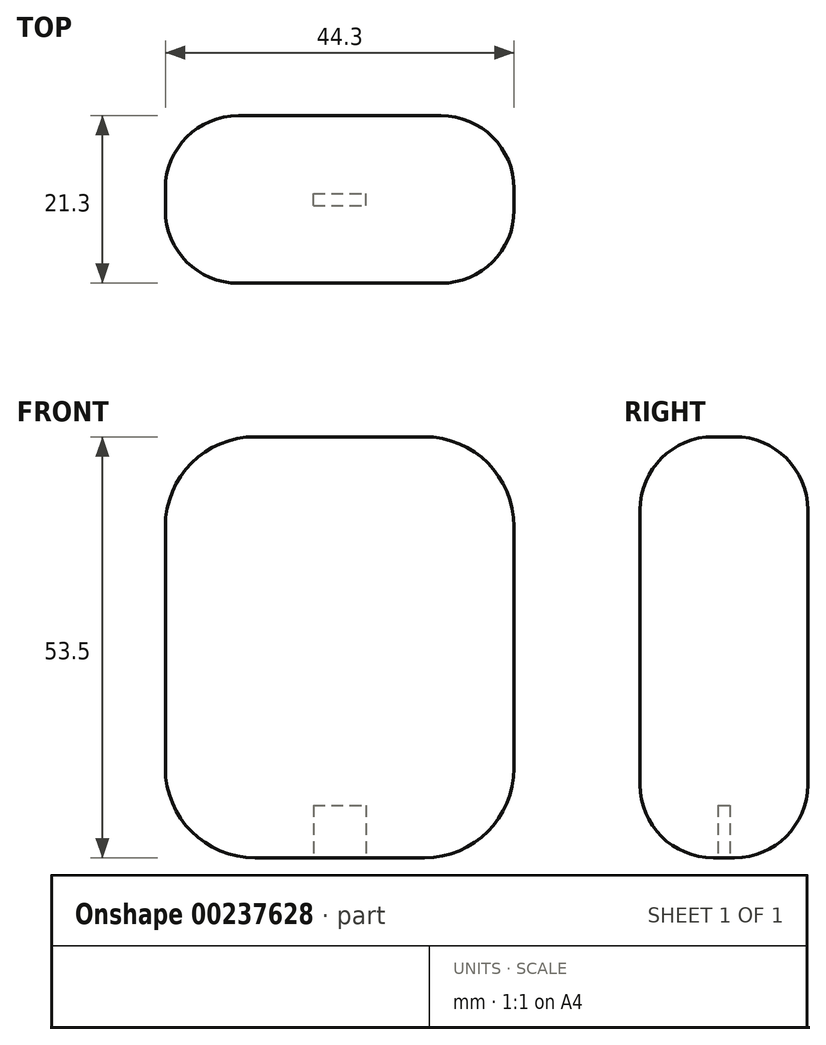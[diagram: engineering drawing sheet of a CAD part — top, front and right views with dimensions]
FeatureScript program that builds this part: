
annotation { "Feature Type Name" : "Feature", "Feature Type Description" : "" }
export const myFeature = defineFeature(function(context is Context, id is Id, definition is map)
    precondition{}
    {
        {
            var Q0;
            Q0=qCreatedBy(makeId("Front.planeOp"),FACE);
            var sketch = newSketch(context, id + "F0", { "sketchPlane" : qUnion([Q0])});
            skLineSegment(sketch, "E0.bottom", {"start": v(0, 0) * mm, "end": v(44.3, 0) * mm});
            skLineSegment(sketch, "E0.top", {"start": v(0, 53.5) * mm, "end": v(44.3, 53.5) * mm});
            skLineSegment(sketch, "E0.left", {"start": v(0, 0) * mm, "end": v(0, 53.5) * mm});
            skLineSegment(sketch, "E0.right", {"start": v(44.3, 0) * mm, "end": v(44.3, 53.5) * mm});
            skSolve(sketch);
        }
        {
            var Q0;
            Q0=makeQuery(id+"F0.imprint","IMPRINT",FACE,{"disambiguationData":[TD([[makeQuery(id+"F0.imprint","IMPRINT",EDGE,{"derivedFrom":sQuery(id+"F0.wireOp",EDGE,"E0.bottom")}),1.0]])]});
            extrude(context, id + "F1", {"entities" : qUnion([Q0]), "depth" : 21.3 * mm});
        }
        {
            var Q0;
            Q0=makeQuery(id+"F1.opExtrude","SWEPT_EDGE",EDGE,{"disambiguationData":[OSD([sQuery(id+"F0.wireOp",EDGE,"E0.bottom"),sQuery(id+"F0.wireOp",EDGE,"E0.right")])]});
            fillet(context, id + "F2", {"entities" : qUnion([Q0]), "radius" : 11.4 * mm, "tangentPropagation" : true, "allowEdgeOverflow" : false});
        }
        {
            var Q0;
            Q0=makeQuery(id+"F1.opExtrude","SWEPT_EDGE",EDGE,{"disambiguationData":[OSD([sQuery(id+"F0.wireOp",EDGE,"E0.bottom"),sQuery(id+"F0.wireOp",EDGE,"E0.left")])]});
            fillet(context, id + "F3", {"entities" : qUnion([Q0]), "radius" : 11.4 * mm, "tangentPropagation" : true, "allowEdgeOverflow" : false});
        }
        {
            var Q0;
            Q0=makeQuery(id+"F1.opExtrude","SWEPT_EDGE",EDGE,{"disambiguationData":[OSD([sQuery(id+"F0.wireOp",EDGE,"E0.top"),sQuery(id+"F0.wireOp",EDGE,"E0.right")])]});
            var Q1;
            Q1=makeQuery(id+"F1.opExtrude","SWEPT_EDGE",EDGE,{"disambiguationData":[OSD([sQuery(id+"F0.wireOp",EDGE,"E0.top"),sQuery(id+"F0.wireOp",EDGE,"E0.left")])]});
            fillet(context, id + "F4", {"entities" : qUnion([Q0, Q1]), "radius" : 11.4 * mm, "tangentPropagation" : true, "allowEdgeOverflow" : false});
        }
        {
            var Q0;
            {var subQ0=sQuery(id+"F0.wireOp",EDGE,"E0.left");var subQ1=sQuery(id+"F0.wireOp",EDGE,"E0.top");Q0=makeQuery(id+"F4.opFillet","BLEND_EDGE",EDGE,{"blendedFrom":[makeQuery(id+"F1.opExtrude","SWEPT_EDGE",EDGE,{"disambiguationData":[OSD([subQ1,subQ0])]}),makeQuery(id+"F1.opExtrude","CAP_FACE",FACE,{"disambiguationData":[OSD([sQuery(id+"F0.wireOp",EDGE,"E0.bottom"),subQ1,subQ0,sQuery(id+"F0.wireOp",EDGE,"E0.right")])],"isStart":false})],"blendedInto":[makeQuery(id+"F1.opExtrude","CAP_FACE",FACE,{"disambiguationData":[OSD([sQuery(id+"F0.wireOp",EDGE,"E0.bottom"),subQ1,subQ0,sQuery(id+"F0.wireOp",EDGE,"E0.right")])],"isStart":false})]});}
            var Q1;
            {var subQ0=sQuery(id+"F0.wireOp",EDGE,"E0.left");var subQ1=sQuery(id+"F0.wireOp",EDGE,"E0.top");Q1=makeQuery(id+"F4.opFillet","BLEND_EDGE",EDGE,{"blendedFrom":[makeQuery(id+"F1.opExtrude","SWEPT_EDGE",EDGE,{"disambiguationData":[OSD([subQ1,subQ0])]}),makeQuery(id+"F1.opExtrude","CAP_FACE",FACE,{"disambiguationData":[OSD([sQuery(id+"F0.wireOp",EDGE,"E0.bottom"),subQ1,subQ0,sQuery(id+"F0.wireOp",EDGE,"E0.right")])],"isStart":true})],"blendedInto":[makeQuery(id+"F1.opExtrude","CAP_FACE",FACE,{"disambiguationData":[OSD([sQuery(id+"F0.wireOp",EDGE,"E0.bottom"),subQ1,subQ0,sQuery(id+"F0.wireOp",EDGE,"E0.right")])],"isStart":true})]});}
            fillet(context, id + "F5", {"entities" : qUnion([Q0, Q1]), "radius" : 9.3 * mm, "tangentPropagation" : true, "allowEdgeOverflow" : false});
        }
        {
            var Q0;
            Q0=makeQuery(id+"F1.opExtrude","SWEPT_FACE",FACE,{"disambiguationData":[OSD([sQuery(id+"F0.wireOp",EDGE,"E0.bottom")])]});
            var sketch = newSketch(context, id + "F6", { "sketchPlane" : qUnion([Q0])});
            skLineSegment(sketch, "E1.bottom", {"start": v(18.8, 11.4) * mm, "end": v(25.5, 11.4) * mm});
            skLineSegment(sketch, "E1.top", {"start": v(18.8, 9.9) * mm, "end": v(25.5, 9.9) * mm});
            skLineSegment(sketch, "E1.left", {"start": v(18.8, 11.4) * mm, "end": v(18.8, 9.9) * mm});
            skLineSegment(sketch, "E1.right", {"start": v(25.5, 11.4) * mm, "end": v(25.5, 9.9) * mm});
            skSolve(sketch);
        }
        {
            var Q0;
            Q0=makeQuery(id+"F6.imprint","IMPRINT",FACE,{"disambiguationData":[TD([[makeQuery(id+"F6.imprint","IMPRINT",EDGE,{"derivedFrom":sQuery(id+"F6.wireOp",EDGE,"E1.bottom")}),-1.0]])]});
            extrude(context, id + "F7", {"entities" : qUnion([Q0]), "operationType" : NewBodyOperationType.REMOVE, "oppositeDirection" : true, "depth" : 6.7 * mm});
        }
    });
